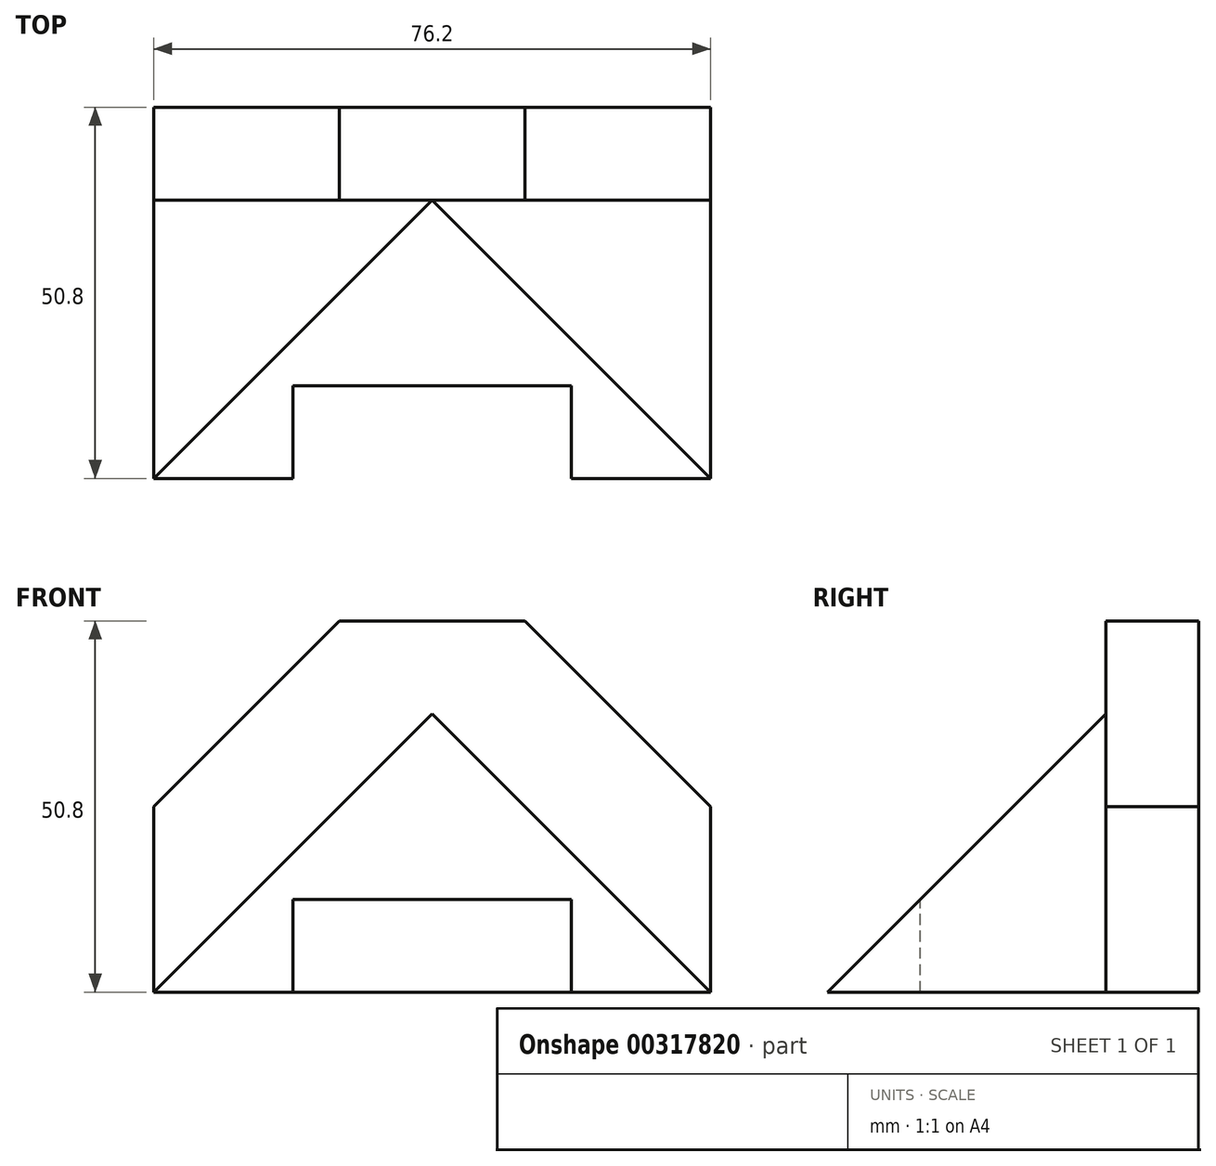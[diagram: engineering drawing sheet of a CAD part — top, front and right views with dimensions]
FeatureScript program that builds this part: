
annotation { "Feature Type Name" : "Feature", "Feature Type Description" : "" }
export const myFeature = defineFeature(function(context is Context, id is Id, definition is map)
    precondition{}
    {
        {
            var Q0;
            Q0=qCreatedBy(makeId("Right.planeOp"),FACE);
            var sketch = newSketch(context, id + "F0", { "sketchPlane" : qUnion([Q0])});
            skLineSegment(sketch, "E0", {"start": v(0, 0) * mm, "end": v(38.1, 0) * mm});
            skLineSegment(sketch, "E1", {"start": v(38.1, 0) * mm, "end": v(38.1, 50.8) * mm});
            skLineSegment(sketch, "E2", {"start": v(38.1, 50.8) * mm, "end": v(50.8, 50.8) * mm});
            skLineSegment(sketch, "E3", {"start": v(38.1, 0) * mm, "end": v(50.8, 0) * mm});
            skLineSegment(sketch, "E4", {"start": v(50.8, 0) * mm, "end": v(50.8, 50.8) * mm});
            skLineSegment(sketch, "E5", {"start": v(0, 0) * mm, "end": v(38.1, 38.1) * mm});
            skSolve(sketch);
        }
        {
            var Q0;
            Q0 = qSketchRegion(id + "F0", true);
            extrude(context, id + "F1", {"entities" : qUnion([Q0]), "depth" : 76.2 * mm});
        }
        {
            var Q0;
            Q0=makeQuery(id+"F1.opExtrude","SWEPT_FACE",FACE,{"disambiguationData":[OSD([sQuery(id+"F0.wireOp",EDGE,"E4")])]});
            var sketch = newSketch(context, id + "F2", { "sketchPlane" : qUnion([Q0])});
            skSolve(sketch);
        }
        {
            var Q0;
            Q0=makeQuery(id+"F1.opExtrude","SWEPT_FACE",FACE,{"disambiguationData":[OSD([sQuery(id+"F0.wireOp",EDGE,"E4")])]});
            var sketch = newSketch(context, id + "F3", { "sketchPlane" : qUnion([Q0])});
            skLineSegment(sketch, "E6", {"start": v(-76.2, 25.4) * mm, "end": v(-50.8, 50.8) * mm});
            skLineSegment(sketch, "E7", {"start": v(-76.2, 50.8) * mm, "end": v(-76.2, 25.4) * mm});
            skLineSegment(sketch, "E8", {"start": v(-76.2, 50.8) * mm, "end": v(-50.8, 50.8) * mm});
            skLineSegment(sketch, "E9", {"start": v(0, 50.8) * mm, "end": v(-25.4, 50.8) * mm});
            skLineSegment(sketch, "E10", {"start": v(-25.4, 50.8) * mm, "end": v(0, 25.4) * mm});
            skLineSegment(sketch, "E11", {"start": v(0, 25.4) * mm, "end": v(0, 50.8) * mm});
            skSolve(sketch);
        }
        {
            var Q0;
            Q0 = qSketchRegion(id + "F3", true);
            extrude(context, id + "F4", {"entities" : qUnion([Q0]), "operationType" : NewBodyOperationType.REMOVE, "endBound" : BoundingType.THROUGH_ALL, "oppositeDirection" : true, "depth" : 25.4 * mm});
        }
        {
            var Q0;
            Q0=makeQuery(id+"F1.opExtrude","SWEPT_FACE",FACE,{"disambiguationData":[OSD([sQuery(id+"F0.wireOp",EDGE,"E4")])]});
            var sketch = newSketch(context, id + "F5", { "sketchPlane" : qUnion([Q0])});
            skLineSegment(sketch, "E12", {"start": v(-76.2, 0) * mm, "end": v(-38.1, 38.1) * mm});
            skLineSegment(sketch, "E13", {"start": v(-38.1, 38.1) * mm, "end": v(0, 0) * mm});
            skLineSegment(sketch, "E14", {"start": v(-76.2, 0) * mm, "end": v(0, 0) * mm});
            skLineSegment(sketch, "E15", {"start": v(-38.1, 38.1) * mm, "end": v(-76.2, 38.1) * mm});
            skLineSegment(sketch, "E16", {"start": v(-76.2, 38.1) * mm, "end": v(-76.2, 0) * mm});
            skLineSegment(sketch, "E17", {"start": v(-38.1, 38.1) * mm, "end": v(0, 38.1) * mm});
            skLineSegment(sketch, "E18", {"start": v(0, 38.1) * mm, "end": v(0, 0) * mm});
            skSolve(sketch);
        }
        {
            var Q0;
            {var subQ0=sQuery(id+"F5.wireOp",EDGE,"E12");Q0=makeQuery(id+"F5.imprint","IMPRINT",FACE,{"disambiguationData":[TD([[makeQuery(id+"F5.imprint","IMPRINT",EDGE,{"derivedFrom":subQ0}),1.0]])]});}
            var Q1;
            {var subQ0=sQuery(id+"F5.wireOp",EDGE,"E13");Q1=makeQuery(id+"F5.imprint","IMPRINT",FACE,{"disambiguationData":[TD([[makeQuery(id+"F5.imprint","IMPRINT",EDGE,{"derivedFrom":subQ0}),1.0]])]});}
            extrude(context, id + "F6", {"entities" : qUnion([Q0, Q1]), "operationType" : NewBodyOperationType.REMOVE, "endBound" : BoundingType.THROUGH_ALL, "oppositeDirection" : true, "depth" : 25.4 * mm, "hasSecondDirection" : true, "secondDirectionOppositeDirection" : true, "secondDirectionDepth" : 12.7 * mm});
        }
        {
            var Q0;
            {var subQ0=sQuery(id+"F0.wireOp",EDGE,"E4");Q0=makeQuery(id+"F2.imprint","IMPRINT",FACE,{"disambiguationData":[TD([[makeQuery(id+"F2.imprint","IMPRINT",EDGE,{"derivedFrom":makeQuery(id+"F1.opExtrude","CAP_EDGE",EDGE,{"disambiguationData":[OSD([subQ0])],"isStart":true})}),1.0]])]});}
            var sketch = newSketch(context, id + "F7", { "sketchPlane" : qUnion([Q0])});
            skLineSegment(sketch, "E19.bottom", {"start": v(-57.15, 0) * mm, "end": v(-19.05, 0) * mm});
            skLineSegment(sketch, "E19.top", {"start": v(-57.15, 12.7) * mm, "end": v(-19.05, 12.7) * mm});
            skLineSegment(sketch, "E19.left", {"start": v(-57.15, 0) * mm, "end": v(-57.15, 12.7) * mm});
            skLineSegment(sketch, "E19.right", {"start": v(-19.05, 0) * mm, "end": v(-19.05, 12.7) * mm});
            skSolve(sketch);
        }
        {
            var Q0;
            Q0 = qSketchRegion(id + "F7", true);
            extrude(context, id + "F8", {"entities" : qUnion([Q0]), "operationType" : NewBodyOperationType.REMOVE, "oppositeDirection" : true, "depth" : 60.2 * mm, "hasSecondDirection" : true, "secondDirectionOppositeDirection" : true, "secondDirectionDepth" : 38.1 * mm});
        }
    });
